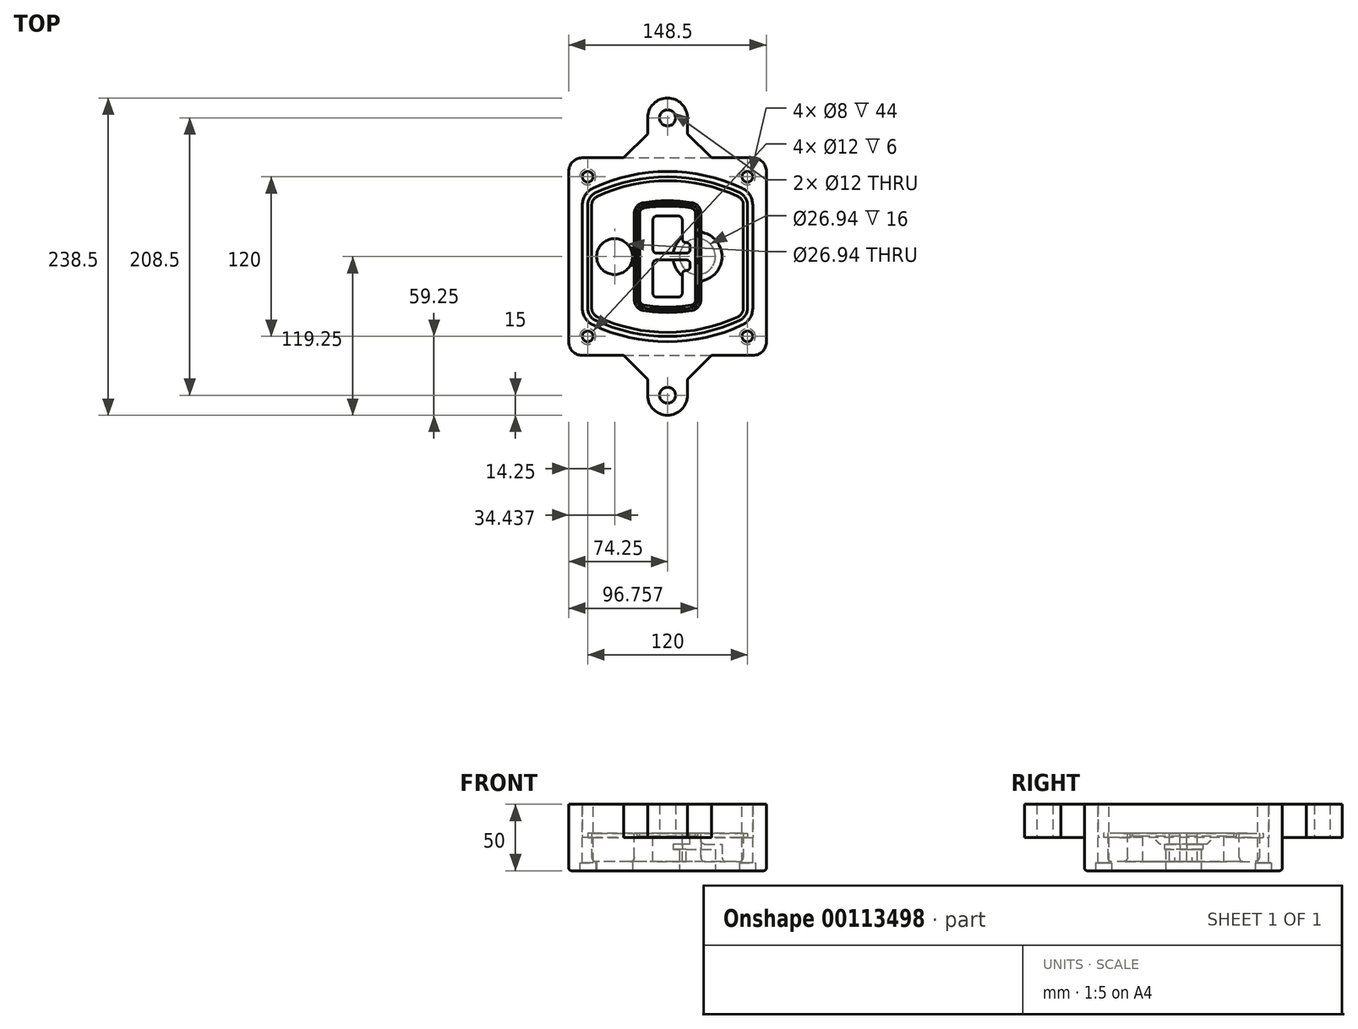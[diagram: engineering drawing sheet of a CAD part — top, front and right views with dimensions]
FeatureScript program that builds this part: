
annotation { "Feature Type Name" : "Feature", "Feature Type Description" : "" }
export const myFeature = defineFeature(function(context is Context, id is Id, definition is map)
    precondition{}
    {
        {
            var Q0;
            Q0=qCreatedBy(makeId("Top.planeOp"),FACE);
            var sketch = newSketch(context, id + "F0", { "sketchPlane" : qUnion([Q0])});
            skPoint(sketch, "E0.rect.middle", {"position": v(0, 0) * mm});
            skLineSegment(sketch, "E1.bottom", {"start": v(-64.25, -74.25) * mm, "end": v(64.25, -74.25) * mm});
            skLineSegment(sketch, "E1.top", {"start": v(-64.25, 74.25) * mm, "end": v(64.25, 74.25) * mm});
            skLineSegment(sketch, "E1.left", {"start": v(-74.25, -64.25) * mm, "end": v(-74.25, 64.25) * mm});
            skLineSegment(sketch, "E1.right", {"start": v(74.25, -64.25) * mm, "end": v(74.25, 64.25) * mm});
            skLineSegment(sketch, "E2", {"start": v(-74.25, 74.25) * mm, "end": v(74.25, -74.25) * mm, "construction": true});
            skLineSegment(sketch, "E3", {"start": v(74.25, 74.25) * mm, "end": v(-74.25, -74.25) * mm, "construction": true});
            skCircle(sketch, "E4", {"center": v(-60, 60) * mm, "radius": 4 * mm});
            skCircle(sketch, "E5", {"center": v(60, 60) * mm, "radius": 4 * mm});
            skCircle(sketch, "E6", {"center": v(60, -60) * mm, "radius": 4 * mm});
            skCircle(sketch, "E7", {"center": v(-60, -60) * mm, "radius": 4 * mm});
            skLineSegment(sketch, "E8", {"start": v(-60, 60) * mm, "end": v(60, 60) * mm, "construction": true});
            skLineSegment(sketch, "E9", {"start": v(60, 60) * mm, "end": v(60, -60) * mm, "construction": true});
            skLineSegment(sketch, "E10", {"start": v(60, -60) * mm, "end": v(-60, -60) * mm, "construction": true});
            skLineSegment(sketch, "E11", {"start": v(-60, -60) * mm, "end": v(-60, 60) * mm, "construction": true});
            skLineSegment(sketch, "E12", {"start": v(-60, 38.83) * mm, "end": v(-60, -38.83) * mm});
            skLineSegment(sketch, "E13", {"start": v(60, 38.83) * mm, "end": v(60, -38.83) * mm});
            skArc(sketch, "E14", {"start": v(54.26, 47.88) * mm, "mid": v(0, 60) * mm, "end": v(-54.26, 47.88) * mm});
            skArc(sketch, "E15", {"start": v(-54.26, -47.88) * mm, "mid": v(0, -60) * mm, "end": v(54.26, -47.88) * mm});
            skLineSegment(sketch, "E16", {"start": v(-60, 0) * mm, "end": v(60, 0) * mm, "construction": true});
            skPoint(sketch, "E17.visualSharp", {"position": v(-60, -45) * mm});
            skArc(sketch, "E17.filletArc", {"start": v(-60, -38.83) * mm, "mid": v(-58.44, -44.2) * mm, "end": v(-54.26, -47.88) * mm});
            skPoint(sketch, "E18.visualSharp", {"position": v(-60, 45) * mm});
            skArc(sketch, "E18.filletArc", {"start": v(-54.26, 47.88) * mm, "mid": v(-58.44, 44.2) * mm, "end": v(-60, 38.83) * mm});
            skPoint(sketch, "E19.visualSharp", {"position": v(60, 45) * mm});
            skArc(sketch, "E19.filletArc", {"start": v(60, 38.83) * mm, "mid": v(58.44, 44.2) * mm, "end": v(54.26, 47.88) * mm});
            skPoint(sketch, "E20.visualSharp", {"position": v(60, -45) * mm});
            skArc(sketch, "E20.filletArc", {"start": v(54.26, -47.88) * mm, "mid": v(58.44, -44.2) * mm, "end": v(60, -38.83) * mm});
            skPoint(sketch, "E21.visualSharp", {"position": v(-74.25, 74.25) * mm});
            skArc(sketch, "E21.filletArc", {"start": v(-64.25, 74.25) * mm, "mid": v(-71.32, 71.32) * mm, "end": v(-74.25, 64.25) * mm});
            skPoint(sketch, "E22.visualSharp", {"position": v(74.25, 74.25) * mm});
            skArc(sketch, "E22.filletArc", {"start": v(74.25, 64.25) * mm, "mid": v(71.32, 71.32) * mm, "end": v(64.25, 74.25) * mm});
            skPoint(sketch, "E23.visualSharp", {"position": v(74.25, -74.25) * mm});
            skArc(sketch, "E23.filletArc", {"start": v(64.25, -74.25) * mm, "mid": v(71.32, -71.32) * mm, "end": v(74.25, -64.25) * mm});
            skPoint(sketch, "E24.visualSharp", {"position": v(-74.25, -74.25) * mm});
            skArc(sketch, "E24.filletArc", {"start": v(-74.25, -64.25) * mm, "mid": v(-71.32, -71.32) * mm, "end": v(-64.25, -74.25) * mm});
            skArc(sketch, "E25.0", {"start": v(57, 38.83) * mm, "mid": v(55.9, 42.58) * mm, "end": v(52.98, 45.17) * mm});
            skLineSegment(sketch, "E25.1", {"start": v(57, 38.83) * mm, "end": v(57, -38.83) * mm});
            skArc(sketch, "E25.2", {"start": v(52.98, -45.17) * mm, "mid": v(55.9, -42.58) * mm, "end": v(57, -38.83) * mm});
            skArc(sketch, "E25.3", {"start": v(-52.98, -45.17) * mm, "mid": v(0, -57) * mm, "end": v(52.98, -45.17) * mm});
            skArc(sketch, "E25.4", {"start": v(-57, -38.83) * mm, "mid": v(-55.9, -42.58) * mm, "end": v(-52.98, -45.17) * mm});
            skArc(sketch, "E25.5", {"start": v(52.98, 45.17) * mm, "mid": v(0, 57) * mm, "end": v(-52.98, 45.17) * mm});
            skLineSegment(sketch, "E25.6", {"start": v(-57, 38.83) * mm, "end": v(-57, -38.83) * mm});
            skArc(sketch, "E25.7", {"start": v(-52.98, 45.17) * mm, "mid": v(-55.9, 42.58) * mm, "end": v(-57, 38.83) * mm});
            skArc(sketch, "E26.0", {"start": v(-55.96, 51.5) * mm, "mid": v(-61.82, 46.33) * mm, "end": v(-64, 38.83) * mm});
            skArc(sketch, "E26.1", {"start": v(55.96, 51.5) * mm, "mid": v(0, 64) * mm, "end": v(-55.96, 51.5) * mm});
            skArc(sketch, "E26.2", {"start": v(64, 38.83) * mm, "mid": v(61.82, 46.33) * mm, "end": v(55.96, 51.5) * mm});
            skLineSegment(sketch, "E26.3", {"start": v(64, 38.83) * mm, "end": v(64, -38.83) * mm});
            skArc(sketch, "E26.4", {"start": v(55.96, -51.5) * mm, "mid": v(61.82, -46.33) * mm, "end": v(64, -38.83) * mm});
            skLineSegment(sketch, "E26.5", {"start": v(-64, 38.83) * mm, "end": v(-64, -38.83) * mm});
            skArc(sketch, "E26.6", {"start": v(-55.96, -51.5) * mm, "mid": v(0, -64) * mm, "end": v(55.96, -51.5) * mm});
            skArc(sketch, "E26.7", {"start": v(-64, -38.83) * mm, "mid": v(-61.82, -46.33) * mm, "end": v(-55.96, -51.5) * mm});
            skLineSegment(sketch, "E27", {"start": v(-33, 74.25) * mm, "end": v(-15, 92.25) * mm});
            skLineSegment(sketch, "E28", {"start": v(-15, 92.25) * mm, "end": v(-15, 104.25) * mm});
            skLineSegment(sketch, "E29", {"start": v(33, 74.25) * mm, "end": v(15, 92.25) * mm});
            skLineSegment(sketch, "E30", {"start": v(15, 92.25) * mm, "end": v(15, 104.25) * mm});
            skArc(sketch, "E31", {"start": v(15, 104.25) * mm, "mid": v(0, 119.25) * mm, "end": v(-15, 104.25) * mm});
            skCircle(sketch, "E32", {"center": v(0, 104.25) * mm, "radius": 6 * mm});
            skLineSegment(sketch, "E33", {"start": v(0, 104.25) * mm, "end": v(0, 74.25) * mm, "construction": true});
            skLineSegment(sketch, "E34", {"start": v(-74.25, 0) * mm, "end": v(74.25, 0) * mm, "construction": true});
            skLineSegment(sketch, "E35.MirrorCS", {"start": v(33, -74.25) * mm, "end": v(15, -92.25) * mm});
            skLineSegment(sketch, "E36.MirrorCS", {"start": v(15, -92.25) * mm, "end": v(15, -104.25) * mm});
            skArc(sketch, "E37.MirrorCS", {"start": v(15, -104.25) * mm, "mid": v(0, -119.25) * mm, "end": v(-15, -104.25) * mm});
            skLineSegment(sketch, "E38.MirrorCS", {"start": v(-15, -92.25) * mm, "end": v(-15, -104.25) * mm});
            skLineSegment(sketch, "E39.MirrorCS", {"start": v(-33, -74.25) * mm, "end": v(-15, -92.25) * mm});
            skCircle(sketch, "E40.MirrorC", {"center": v(0, -104.25) * mm, "radius": 6 * mm});
            skLineSegment(sketch, "E41.MirrorCS", {"start": v(0, -104.25) * mm, "end": v(0, -74.25) * mm, "construction": true});
            skSolve(sketch);
        }
        {
            var Q0;
            Q0=makeQuery(id+"F0.imprint","IMPRINT",FACE,{"disambiguationData":[TD([[makeQuery(id+"F0.imprint","IMPRINT",EDGE,{"derivedFrom":sQuery(id+"F0.wireOp",EDGE,"E1.bottom")}),1.0]])]});
            var Q1;
            Q1=makeQuery(id+"F0.imprint","IMPRINT",FACE,{"disambiguationData":[TD([[makeQuery(id+"F0.imprint","IMPRINT",EDGE,{"derivedFrom":sQuery(id+"F0.wireOp",EDGE,"E12")}),1.0]])]});
            var Q2;
            Q2=makeQuery(id+"F0.imprint","IMPRINT",FACE,{"disambiguationData":[TD([[makeQuery(id+"F0.imprint","IMPRINT",EDGE,{"derivedFrom":sQuery(id+"F0.wireOp",EDGE,"E25.0")}),1.0]])]});
            var Q3;
            Q3=makeQuery(id+"F0.imprint","IMPRINT",FACE,{"disambiguationData":[TD([[makeQuery(id+"F0.imprint","IMPRINT",EDGE,{"derivedFrom":sQuery(id+"F0.wireOp",EDGE,"E12")}),-1.0]])]});
            extrude(context, id + "F1", {"entities" : qUnion([Q0, Q1, Q2, Q3]), "oppositeDirection" : true, "depth" : 25 * mm});
        }
        {
            var Q0;
            Q0=makeQuery(id+"F0.imprint","IMPRINT",FACE,{"disambiguationData":[TD([[makeQuery(id+"F0.imprint","IMPRINT",EDGE,{"derivedFrom":sQuery(id+"F0.wireOp",EDGE,"E12")}),1.0]])]});
            extrude(context, id + "F2", {"entities" : qUnion([Q0]), "operationType" : NewBodyOperationType.ADD, "depth" : 3 * mm});
        }
        {
            var Q0;
            Q0=makeQuery(id+"F0.imprint","IMPRINT",FACE,{"disambiguationData":[TD([[makeQuery(id+"F0.imprint","IMPRINT",EDGE,{"derivedFrom":sQuery(id+"F0.wireOp",EDGE,"E25.0")}),1.0]])]});
            extrude(context, id + "F3", {"entities" : qUnion([Q0]), "operationType" : NewBodyOperationType.REMOVE, "oppositeDirection" : true, "depth" : 18 * mm});
        }
        {
            var Q0;
            Q0=makeQuery(id+"F2.opExtrude","CAP_FACE",FACE,{"disambiguationData":[OSD([sQuery(id+"F0.wireOp",EDGE,"E12"),sQuery(id+"F0.wireOp",EDGE,"E13"),sQuery(id+"F0.wireOp",EDGE,"E14"),sQuery(id+"F0.wireOp",EDGE,"E15"),sQuery(id+"F0.wireOp",EDGE,"E17.filletArc"),sQuery(id+"F0.wireOp",EDGE,"E18.filletArc"),sQuery(id+"F0.wireOp",EDGE,"E19.filletArc"),sQuery(id+"F0.wireOp",EDGE,"E20.filletArc"),sQuery(id+"F0.wireOp",EDGE,"E25.0"),sQuery(id+"F0.wireOp",EDGE,"E25.1"),sQuery(id+"F0.wireOp",EDGE,"E25.2"),sQuery(id+"F0.wireOp",EDGE,"E25.3"),sQuery(id+"F0.wireOp",EDGE,"E25.4"),sQuery(id+"F0.wireOp",EDGE,"E25.5"),sQuery(id+"F0.wireOp",EDGE,"E25.6"),sQuery(id+"F0.wireOp",EDGE,"E25.7")])],"isStart":false});
            var sketch = newSketch(context, id + "F4", { "sketchPlane" : qUnion([Q0])});
            skArc(sketch, "E42.0", {"start": v(-18.34, -40.45) * mm, "mid": v(0, -42) * mm, "end": v(18.34, -40.45) * mm});
            skArc(sketch, "E43.0", {"start": v(18.34, 40.45) * mm, "mid": v(0, 42) * mm, "end": v(-18.34, 40.45) * mm});
            skLineSegment(sketch, "E44", {"start": v(-25, 32.57) * mm, "end": v(-25, -32.57) * mm});
            skLineSegment(sketch, "E45", {"start": v(25, 32.57) * mm, "end": v(25, -32.57) * mm});
            skLineSegment(sketch, "E46", {"start": v(-25, 39.1) * mm, "end": v(25, 39.1) * mm, "construction": true});
            skLineSegment(sketch, "E47", {"start": v(-25, -39.1) * mm, "end": v(25, -39.1) * mm, "construction": true});
            skPoint(sketch, "E48.visualSharp", {"position": v(-25, 39.1) * mm});
            skArc(sketch, "E48.filletArc", {"start": v(-18.34, 40.45) * mm, "mid": v(-23.11, 37.73) * mm, "end": v(-25, 32.57) * mm});
            skPoint(sketch, "E49.visualSharp", {"position": v(25, 39.1) * mm});
            skArc(sketch, "E49.filletArc", {"start": v(25, 32.57) * mm, "mid": v(23.11, 37.73) * mm, "end": v(18.34, 40.45) * mm});
            skPoint(sketch, "E50.visualSharp", {"position": v(25, -39.1) * mm});
            skArc(sketch, "E50.filletArc", {"start": v(18.34, -40.45) * mm, "mid": v(23.11, -37.73) * mm, "end": v(25, -32.57) * mm});
            skPoint(sketch, "E51.visualSharp", {"position": v(-25, -39.1) * mm});
            skArc(sketch, "E51.filletArc", {"start": v(-25, -32.57) * mm, "mid": v(-23.11, -37.73) * mm, "end": v(-18.34, -40.45) * mm});
            skArc(sketch, "E52.0", {"start": v(52.98, 45.17) * mm, "mid": v(0, 57) * mm, "end": v(-52.98, 45.17) * mm});
            skArc(sketch, "E52.1", {"start": v(-52.98, 45.17) * mm, "mid": v(-55.9, 42.58) * mm, "end": v(-57, 38.83) * mm});
            skLineSegment(sketch, "E52.2", {"start": v(-57, 38.83) * mm, "end": v(-57, -38.83) * mm});
            skArc(sketch, "E52.3", {"start": v(-57, -38.83) * mm, "mid": v(-55.9, -42.58) * mm, "end": v(-52.98, -45.17) * mm});
            skArc(sketch, "E52.4", {"start": v(-52.98, -45.17) * mm, "mid": v(0, -57) * mm, "end": v(52.98, -45.17) * mm});
            skArc(sketch, "E52.5", {"start": v(52.98, -45.17) * mm, "mid": v(55.9, -42.58) * mm, "end": v(57, -38.83) * mm});
            skLineSegment(sketch, "E52.6", {"start": v(57, 38.83) * mm, "end": v(57, -38.83) * mm});
            skArc(sketch, "E52.7", {"start": v(57, 38.83) * mm, "mid": v(55.9, 42.58) * mm, "end": v(52.98, 45.17) * mm});
            skLineSegment(sketch, "E53.0", {"start": v(23, 32.57) * mm, "end": v(23, -32.57) * mm});
            skArc(sketch, "E53.1", {"start": v(18, -38.48) * mm, "mid": v(21.58, -36.44) * mm, "end": v(23, -32.57) * mm});
            skArc(sketch, "E53.2", {"start": v(-18, -38.48) * mm, "mid": v(0, -40) * mm, "end": v(18, -38.48) * mm});
            skArc(sketch, "E53.3", {"start": v(-23, -32.57) * mm, "mid": v(-21.58, -36.44) * mm, "end": v(-18, -38.48) * mm});
            skLineSegment(sketch, "E53.4", {"start": v(-23, 32.57) * mm, "end": v(-23, -32.57) * mm});
            skArc(sketch, "E53.5", {"start": v(23, 32.57) * mm, "mid": v(21.58, 36.44) * mm, "end": v(18, 38.48) * mm});
            skArc(sketch, "E53.6", {"start": v(-18, 38.48) * mm, "mid": v(-21.58, 36.44) * mm, "end": v(-23, 32.57) * mm});
            skArc(sketch, "E53.7", {"start": v(18, 38.48) * mm, "mid": v(0, 40) * mm, "end": v(-18, 38.48) * mm});
            skArc(sketch, "E54.0", {"start": v(21, 32.57) * mm, "mid": v(20.06, 35.15) * mm, "end": v(17.67, 36.5) * mm});
            skLineSegment(sketch, "E54.1", {"start": v(21, 32.57) * mm, "end": v(21, -32.57) * mm});
            skArc(sketch, "E54.2", {"start": v(17.67, -36.5) * mm, "mid": v(20.06, -35.15) * mm, "end": v(21, -32.57) * mm});
            skArc(sketch, "E54.3", {"start": v(-17.67, -36.5) * mm, "mid": v(0, -38) * mm, "end": v(17.67, -36.5) * mm});
            skArc(sketch, "E54.4", {"start": v(-21, -32.57) * mm, "mid": v(-20.06, -35.15) * mm, "end": v(-17.67, -36.5) * mm});
            skArc(sketch, "E54.5", {"start": v(17.67, 36.5) * mm, "mid": v(0, 38) * mm, "end": v(-17.67, 36.5) * mm});
            skLineSegment(sketch, "E54.6", {"start": v(-21, 32.57) * mm, "end": v(-21, -32.57) * mm});
            skArc(sketch, "E54.7", {"start": v(-17.67, 36.5) * mm, "mid": v(-20.06, 35.15) * mm, "end": v(-21, 32.57) * mm});
            skLineSegment(sketch, "E55", {"start": v(-25, 0) * mm, "end": v(25, 0) * mm, "construction": true});
            skLineSegment(sketch, "E56", {"start": v(-11, 5.5) * mm, "end": v(-11, 27.5) * mm});
            skLineSegment(sketch, "E57", {"start": v(-8, 30.5) * mm, "end": v(8, 30.5) * mm});
            skLineSegment(sketch, "E58", {"start": v(11, 27.5) * mm, "end": v(11, 13.5) * mm});
            skLineSegment(sketch, "E59", {"start": v(14, 10.5) * mm, "end": v(14, 10.5) * mm});
            skLineSegment(sketch, "E60", {"start": v(17, 7.5) * mm, "end": v(17, 5.5) * mm});
            skLineSegment(sketch, "E61", {"start": v(14, 2.5) * mm, "end": v(-8, 2.5) * mm});
            skPoint(sketch, "E62.visualSharp", {"position": v(-11, 30.5) * mm});
            skArc(sketch, "E62.filletArc", {"start": v(-8, 30.5) * mm, "mid": v(-10.12, 29.62) * mm, "end": v(-11, 27.5) * mm});
            skPoint(sketch, "E63.visualSharp", {"position": v(11, 30.5) * mm});
            skArc(sketch, "E63.filletArc", {"start": v(11, 27.5) * mm, "mid": v(10.12, 29.62) * mm, "end": v(8, 30.5) * mm});
            skPoint(sketch, "E64.visualSharp", {"position": v(11, 10.5) * mm});
            skArc(sketch, "E64.filletArc", {"start": v(11, 13.5) * mm, "mid": v(11.88, 11.38) * mm, "end": v(14, 10.5) * mm});
            skPoint(sketch, "E65.visualSharp", {"position": v(17, 10.5) * mm});
            skArc(sketch, "E65.filletArc", {"start": v(17, 7.5) * mm, "mid": v(16.12, 9.62) * mm, "end": v(14, 10.5) * mm});
            skPoint(sketch, "E66.visualSharp", {"position": v(17, 2.5) * mm});
            skArc(sketch, "E66.filletArc", {"start": v(14, 2.5) * mm, "mid": v(16.12, 3.38) * mm, "end": v(17, 5.5) * mm});
            skPoint(sketch, "E67.visualSharp", {"position": v(-11, 2.5) * mm});
            skArc(sketch, "E67.filletArc", {"start": v(-11, 5.5) * mm, "mid": v(-10.12, 3.38) * mm, "end": v(-8, 2.5) * mm});
            skLineSegment(sketch, "E68.0.MirrorCS", {"start": v(14, -2.5) * mm, "end": v(-8, -2.5) * mm});
            skArc(sketch, "E69.0.MirrorCS", {"start": v(-11, -5.5) * mm, "mid": v(-10.12, -3.38) * mm, "end": v(-8, -2.5) * mm});
            skLineSegment(sketch, "E70.0.MirrorCS", {"start": v(-11, -5.5) * mm, "end": v(-11, -27.5) * mm});
            skArc(sketch, "E71.0.MirrorCS", {"start": v(-8, -30.5) * mm, "mid": v(-10.12, -29.62) * mm, "end": v(-11, -27.5) * mm});
            skLineSegment(sketch, "E72.0.MirrorCS", {"start": v(-8, -30.5) * mm, "end": v(8, -30.5) * mm});
            skArc(sketch, "E73.0.MirrorCS", {"start": v(11, -27.5) * mm, "mid": v(10.12, -29.62) * mm, "end": v(8, -30.5) * mm});
            skLineSegment(sketch, "E74.0.MirrorCS", {"start": v(11, -27.5) * mm, "end": v(11, -13.5) * mm});
            skArc(sketch, "E75.0.MirrorCS", {"start": v(11, -13.5) * mm, "mid": v(11.88, -11.38) * mm, "end": v(14, -10.5) * mm});
            skArc(sketch, "E76.0.MirrorCS", {"start": v(17, -7.5) * mm, "mid": v(16.12, -9.62) * mm, "end": v(14, -10.5) * mm});
            skLineSegment(sketch, "E77.0.MirrorCS", {"start": v(17, -7.5) * mm, "end": v(17, -5.5) * mm});
            skArc(sketch, "E78.0.MirrorCS", {"start": v(14, -2.5) * mm, "mid": v(16.12, -3.38) * mm, "end": v(17, -5.5) * mm});
            skSolve(sketch);
        }
        {
            var Q0;
            Q0=makeQuery(id+"F4.imprint","IMPRINT",FACE,{"disambiguationData":[TD([[makeQuery(id+"F4.imprint","IMPRINT",EDGE,{"derivedFrom":sQuery(id+"F4.wireOp",EDGE,"E42.0")}),1.0]])]});
            var Q1;
            Q1=makeQuery(id+"F4.imprint","IMPRINT",FACE,{"disambiguationData":[TD([[makeQuery(id+"F4.imprint","IMPRINT",EDGE,{"derivedFrom":sQuery(id+"F4.wireOp",EDGE,"E53.0")}),-1.0]])]});
            var Q2;
            Q2=makeQuery(id+"F4.imprint","IMPRINT",FACE,{"disambiguationData":[TD([[makeQuery(id+"F4.imprint","IMPRINT",EDGE,{"derivedFrom":sQuery(id+"F4.wireOp",EDGE,"E54.0")}),1.0]])]});
            extrude(context, id + "F5", {"entities" : qUnion([Q0, Q1, Q2]), "operationType" : NewBodyOperationType.ADD, "endBound" : BoundingType.UP_TO_NEXT, "oppositeDirection" : true, "depth" : 25 * mm});
        }
        {
            var Q0;
            Q0=makeQuery(id+"F4.imprint","IMPRINT",FACE,{"disambiguationData":[TD([[makeQuery(id+"F4.imprint","IMPRINT",EDGE,{"derivedFrom":sQuery(id+"F4.wireOp",EDGE,"E53.0")}),-1.0]])]});
            extrude(context, id + "F6", {"entities" : qUnion([Q0]), "operationType" : NewBodyOperationType.REMOVE, "oppositeDirection" : true, "depth" : 2 * mm});
        }
        {
            var Q0;
            Q0=makeQuery(id+"F1.opExtrude","CAP_FACE",FACE,{"disambiguationData":[OSD([sQuery(id+"F0.wireOp",EDGE,"E1.bottom"),sQuery(id+"F0.wireOp",EDGE,"E1.top"),sQuery(id+"F0.wireOp",EDGE,"E1.left"),sQuery(id+"F0.wireOp",EDGE,"E1.right"),sQuery(id+"F0.wireOp",EDGE,"E4"),sQuery(id+"F0.wireOp",EDGE,"E5"),sQuery(id+"F0.wireOp",EDGE,"E6"),sQuery(id+"F0.wireOp",EDGE,"E7"),sQuery(id+"F0.wireOp",EDGE,"E21.filletArc"),sQuery(id+"F0.wireOp",EDGE,"E22.filletArc"),sQuery(id+"F0.wireOp",EDGE,"E23.filletArc"),sQuery(id+"F0.wireOp",EDGE,"E24.filletArc")])],"isStart":false});
            var sketch = newSketch(context, id + "F7", { "sketchPlane" : qUnion([Q0])});
            skCircle(sketch, "E79", {"center": v(22.5, 0) * mm, "radius": 13.47 * mm});
            skCircle(sketch, "E80", {"center": v(-39.81, 0) * mm, "radius": 13.47 * mm});
            skLineSegment(sketch, "E81", {"start": v(74.25, 0) * mm, "end": v(-74.25, 0) * mm});
            skCircle(sketch, "E82", {"center": v(22.5, 0) * mm, "radius": 18.47 * mm});
            skCircle(sketch, "E83", {"center": v(60, -60) * mm, "radius": 6 * mm});
            skCircle(sketch, "E84", {"center": v(-60, -60) * mm, "radius": 6 * mm});
            skCircle(sketch, "E85", {"center": v(-60, 60) * mm, "radius": 6 * mm});
            skCircle(sketch, "E86", {"center": v(60, 60) * mm, "radius": 6 * mm});
            skSolve(sketch);
        }
        {
            var Q0;
            {var subQ1=sQuery(id+"F7.wireOp",EDGE,"E81");var subQ4=sQuery(id+"F7.wireOp",EDGE,"E79");var subQ6=makeQuery(id+"F7.imprint","INTERSECT",VERTEX,{"disambiguationData":[OD(0.0)],"derivedFrom":[subQ4,subQ1]});Q0=makeQuery(id+"F7.imprint","IMPRINT",FACE,{"disambiguationData":[TD([[makeQuery(id+"F7.imprint","IMPRINT",EDGE,{"disambiguationData":[TD([[subQ6,-1.0]])],"derivedFrom":subQ4}),-1.0]])]});}
            var Q1;
            {var subQ0=sQuery(id+"F7.wireOp",EDGE,"E81");var subQ1=sQuery(id+"F7.wireOp",EDGE,"E79");var subQ3=makeQuery(id+"F7.imprint","INTERSECT",VERTEX,{"disambiguationData":[OD(0.0)],"derivedFrom":[subQ1,subQ0]});Q1=makeQuery(id+"F7.imprint","IMPRINT",FACE,{"disambiguationData":[TD([[makeQuery(id+"F7.imprint","IMPRINT",EDGE,{"disambiguationData":[TD([[subQ3,-1.0]])],"derivedFrom":subQ1}),1.0]])]});}
            var Q2;
            {var subQ0=sQuery(id+"F7.wireOp",EDGE,"E81");var subQ1=sQuery(id+"F7.wireOp",EDGE,"E79");var subQ3=makeQuery(id+"F7.imprint","INTERSECT",VERTEX,{"disambiguationData":[OD(0.0)],"derivedFrom":[subQ1,subQ0]});Q2=makeQuery(id+"F7.imprint","IMPRINT",FACE,{"disambiguationData":[TD([[makeQuery(id+"F7.imprint","IMPRINT",EDGE,{"disambiguationData":[TD([[subQ3,1.0]])],"derivedFrom":subQ1}),1.0]])]});}
            var Q3;
            {var subQ1=sQuery(id+"F7.wireOp",EDGE,"E81");var subQ4=sQuery(id+"F7.wireOp",EDGE,"E79");var subQ6=makeQuery(id+"F7.imprint","INTERSECT",VERTEX,{"disambiguationData":[OD(0.0)],"derivedFrom":[subQ4,subQ1]});Q3=makeQuery(id+"F7.imprint","IMPRINT",FACE,{"disambiguationData":[TD([[makeQuery(id+"F7.imprint","IMPRINT",EDGE,{"disambiguationData":[TD([[subQ6,1.0]])],"derivedFrom":subQ4}),-1.0]])]});}
            extrude(context, id + "F8", {"entities" : qUnion([Q0, Q1, Q2, Q3]), "operationType" : NewBodyOperationType.ADD, "oppositeDirection" : true, "depth" : 20 * mm});
        }
        {
            var Q0;
            {var subQ0=sQuery(id+"F7.wireOp",EDGE,"E81");var subQ1=sQuery(id+"F7.wireOp",EDGE,"E79");var subQ3=makeQuery(id+"F7.imprint","INTERSECT",VERTEX,{"disambiguationData":[OD(0.0)],"derivedFrom":[subQ1,subQ0]});Q0=makeQuery(id+"F7.imprint","IMPRINT",FACE,{"disambiguationData":[TD([[makeQuery(id+"F7.imprint","IMPRINT",EDGE,{"disambiguationData":[TD([[subQ3,-1.0]])],"derivedFrom":subQ1}),1.0]])]});}
            var Q1;
            {var subQ0=sQuery(id+"F7.wireOp",EDGE,"E81");var subQ1=sQuery(id+"F7.wireOp",EDGE,"E79");var subQ3=makeQuery(id+"F7.imprint","INTERSECT",VERTEX,{"disambiguationData":[OD(0.0)],"derivedFrom":[subQ1,subQ0]});Q1=makeQuery(id+"F7.imprint","IMPRINT",FACE,{"disambiguationData":[TD([[makeQuery(id+"F7.imprint","IMPRINT",EDGE,{"disambiguationData":[TD([[subQ3,1.0]])],"derivedFrom":subQ1}),1.0]])]});}
            extrude(context, id + "F9", {"entities" : qUnion([Q0, Q1]), "operationType" : NewBodyOperationType.REMOVE, "oppositeDirection" : true, "depth" : 16 * mm});
        }
        {
            var Q0;
            {var subQ0=sQuery(id+"F7.wireOp",EDGE,"E81");var subQ1=sQuery(id+"F7.wireOp",EDGE,"E80");var subQ3=makeQuery(id+"F7.imprint","INTERSECT",VERTEX,{"disambiguationData":[OD(0.0)],"derivedFrom":[subQ1,subQ0]});Q0=makeQuery(id+"F7.imprint","IMPRINT",FACE,{"disambiguationData":[TD([[makeQuery(id+"F7.imprint","IMPRINT",EDGE,{"disambiguationData":[TD([[subQ3,-1.0]])],"derivedFrom":subQ1}),1.0]])]});}
            var Q1;
            {var subQ0=sQuery(id+"F7.wireOp",EDGE,"E81");var subQ1=sQuery(id+"F7.wireOp",EDGE,"E80");var subQ3=makeQuery(id+"F7.imprint","INTERSECT",VERTEX,{"disambiguationData":[OD(0.0)],"derivedFrom":[subQ1,subQ0]});Q1=makeQuery(id+"F7.imprint","IMPRINT",FACE,{"disambiguationData":[TD([[makeQuery(id+"F7.imprint","IMPRINT",EDGE,{"disambiguationData":[TD([[subQ3,1.0]])],"derivedFrom":subQ1}),1.0]])]});}
            extrude(context, id + "F10", {"entities" : qUnion([Q0, Q1]), "operationType" : NewBodyOperationType.REMOVE, "oppositeDirection" : true, "depth" : 25 * mm});
        }
        {
            var Q0;
            Q0=makeQuery(id+"F7.imprint","IMPRINT",FACE,{"disambiguationData":[TD([[makeQuery(id+"F7.imprint","IMPRINT",EDGE,{"derivedFrom":sQuery(id+"F7.wireOp",EDGE,"E83")}),1.0]])]});
            var Q1;
            Q1=makeQuery(id+"F7.imprint","IMPRINT",FACE,{"disambiguationData":[TD([[makeQuery(id+"F7.imprint","IMPRINT",EDGE,{"derivedFrom":makeQuery(id+"F1.opExtrude","CAP_EDGE",EDGE,{"disambiguationData":[OSD([sQuery(id+"F0.wireOp",EDGE,"E5")])],"isStart":false})}),-1.0]])]});
            var Q2;
            Q2=makeQuery(id+"F7.imprint","IMPRINT",FACE,{"disambiguationData":[TD([[makeQuery(id+"F7.imprint","IMPRINT",EDGE,{"derivedFrom":sQuery(id+"F7.wireOp",EDGE,"E84")}),1.0]])]});
            var Q3;
            Q3=makeQuery(id+"F7.imprint","IMPRINT",FACE,{"disambiguationData":[TD([[makeQuery(id+"F7.imprint","IMPRINT",EDGE,{"derivedFrom":makeQuery(id+"F1.opExtrude","CAP_EDGE",EDGE,{"disambiguationData":[OSD([sQuery(id+"F0.wireOp",EDGE,"E4")])],"isStart":false})}),-1.0]])]});
            var Q4;
            Q4=makeQuery(id+"F7.imprint","IMPRINT",FACE,{"disambiguationData":[TD([[makeQuery(id+"F7.imprint","IMPRINT",EDGE,{"derivedFrom":sQuery(id+"F7.wireOp",EDGE,"E85")}),1.0]])]});
            var Q5;
            Q5=makeQuery(id+"F7.imprint","IMPRINT",FACE,{"disambiguationData":[TD([[makeQuery(id+"F7.imprint","IMPRINT",EDGE,{"derivedFrom":makeQuery(id+"F1.opExtrude","CAP_EDGE",EDGE,{"disambiguationData":[OSD([sQuery(id+"F0.wireOp",EDGE,"E7")])],"isStart":false})}),-1.0]])]});
            var Q6;
            Q6=makeQuery(id+"F7.imprint","IMPRINT",FACE,{"disambiguationData":[TD([[makeQuery(id+"F7.imprint","IMPRINT",EDGE,{"derivedFrom":sQuery(id+"F7.wireOp",EDGE,"E86")}),1.0]])]});
            var Q7;
            Q7=makeQuery(id+"F7.imprint","IMPRINT",FACE,{"disambiguationData":[TD([[makeQuery(id+"F7.imprint","IMPRINT",EDGE,{"derivedFrom":makeQuery(id+"F1.opExtrude","CAP_EDGE",EDGE,{"disambiguationData":[OSD([sQuery(id+"F0.wireOp",EDGE,"E6")])],"isStart":false})}),-1.0]])]});
            extrude(context, id + "F11", {"entities" : qUnion([Q0, Q1, Q2, Q3, Q4, Q5, Q6, Q7]), "operationType" : NewBodyOperationType.REMOVE, "oppositeDirection" : true, "depth" : 6 * mm});
        }
        {
            var Q0;
            Q0=makeQuery(id+"F9.boolean.opBoolean","COPY",FACE,{"derivedFrom":makeQuery(id+"F9.opExtrude","CAP_FACE",FACE,{"disambiguationData":[OSD([sQuery(id+"F7.wireOp",EDGE,"E79")])],"isStart":false})});
            var sketch = newSketch(context, id + "F12", { "sketchPlane" : qUnion([Q0])});
            skArc(sketch, "E87.0", {"start": v(11, 14.45) * mm, "mid": v(6.45, 9.13) * mm, "end": v(4.2, 2.5) * mm});
            skArc(sketch, "E87.1", {"start": v(4.2, -2.5) * mm, "mid": v(6.45, -9.13) * mm, "end": v(11, -14.45) * mm});
            skLineSegment(sketch, "E88", {"start": v(4.2, -2.5) * mm, "end": v(14, -2.5) * mm});
            skLineSegment(sketch, "E89.0", {"start": v(14, 2.5) * mm, "end": v(4.2, 2.5) * mm});
            skArc(sketch, "E89.1", {"start": v(14, 2.5) * mm, "mid": v(16.12, 3.38) * mm, "end": v(17, 5.5) * mm});
            skLineSegment(sketch, "E89.2", {"start": v(17, 7.5) * mm, "end": v(17, 5.5) * mm});
            skArc(sketch, "E89.3", {"start": v(17, 7.5) * mm, "mid": v(16.12, 9.62) * mm, "end": v(14, 10.5) * mm});
            skArc(sketch, "E89.4", {"start": v(11, 13.5) * mm, "mid": v(11.88, 11.38) * mm, "end": v(14, 10.5) * mm});
            skLineSegment(sketch, "E89.5", {"start": v(11, 14.45) * mm, "end": v(11, 13.5) * mm});
            skLineSegment(sketch, "E89.7", {"start": v(14, -2.5) * mm, "end": v(4.2, -2.5) * mm});
            skArc(sketch, "E89.8", {"start": v(14, -2.5) * mm, "mid": v(16.12, -3.38) * mm, "end": v(17, -5.5) * mm});
            skLineSegment(sketch, "E89.9", {"start": v(17, -7.5) * mm, "end": v(17, -5.5) * mm});
            skArc(sketch, "E89.10", {"start": v(17, -7.5) * mm, "mid": v(16.12, -9.62) * mm, "end": v(14, -10.5) * mm});
            skArc(sketch, "E89.11", {"start": v(11, -13.5) * mm, "mid": v(11.88, -11.38) * mm, "end": v(14, -10.5) * mm});
            skLineSegment(sketch, "E89.12", {"start": v(11, -14.45) * mm, "end": v(11, -13.5) * mm});
            skPoint(sketch, "E90.orphan", {"position": v(11, -27.5) * mm});
            skPoint(sketch, "E91.orphan", {"position": v(-8, -2.5) * mm});
            skPoint(sketch, "E92.orphan", {"position": v(-8, 2.5) * mm});
            skPoint(sketch, "E93.orphan", {"position": v(11, 27.5) * mm});
            skSolve(sketch);
        }
        {
            var Q0;
            {var subQ7=sQuery(id+"F12.wireOp",EDGE,"E87.0");var subQ14=sQuery(id+"F12.wireOp",EDGE,"E87.1");var subQ16=sQuery(id+"F12.wireOp",EDGE,"E89.1");var subQ18=sQuery(id+"F12.wireOp",EDGE,"E89.8");Q0=qUnion([makeQuery(id+"F12.imprint","IMPRINT",FACE,{"disambiguationData":[TD([[makeQuery(id+"F12.imprint","IMPRINT",EDGE,{"derivedFrom":subQ7}),1.0]])]}),makeQuery(id+"F12.imprint","IMPRINT",FACE,{"disambiguationData":[TD([[makeQuery(id+"F12.imprint","IMPRINT",EDGE,{"derivedFrom":subQ14}),1.0]])]}),makeQuery(id+"F12.imprint","IMPRINT",FACE,{"disambiguationData":[TD([[makeQuery(id+"F12.imprint","IMPRINT",EDGE,{"derivedFrom":subQ16}),1.0]])]}),makeQuery(id+"F12.imprint","IMPRINT",FACE,{"disambiguationData":[TD([[makeQuery(id+"F12.imprint","IMPRINT",EDGE,{"derivedFrom":subQ18}),-1.0]])]})]);}
            var Q1;
            Q1=makeQuery(id+"F5.boolean.opBoolean","SPLIT",FACE,{"disambiguationData":[TD([makeQuery(id+"F5.opExtrude","SWEPT_FACE",FACE,{"disambiguationData":[OSD([sQuery(id+"F4.wireOp",EDGE,"E56")])]})])],"derivedFrom":makeQuery(id+"F3.boolean.opBoolean","COPY",FACE,{"derivedFrom":makeQuery(id+"F3.opExtrude","CAP_FACE",FACE,{"disambiguationData":[OSD([sQuery(id+"F0.wireOp",EDGE,"E25.0"),sQuery(id+"F0.wireOp",EDGE,"E25.1"),sQuery(id+"F0.wireOp",EDGE,"E25.2"),sQuery(id+"F0.wireOp",EDGE,"E25.3"),sQuery(id+"F0.wireOp",EDGE,"E25.4"),sQuery(id+"F0.wireOp",EDGE,"E25.5"),sQuery(id+"F0.wireOp",EDGE,"E25.6"),sQuery(id+"F0.wireOp",EDGE,"E25.7")])],"isStart":false})})});
            extrude(context, id + "F13", {"entities" : qUnion([Q0]), "operationType" : NewBodyOperationType.REMOVE, "endBound" : BoundingType.UP_TO_SURFACE, "endBoundEntityFace" : qUnion([Q1]), "depth" : 25 * mm});
        }
        {
            var Q0;
            Q0=makeQuery(id+"F3.boolean.opBoolean","COPY",EDGE,{"derivedFrom":makeQuery(id+"F3.opExtrude","CAP_EDGE",EDGE,{"disambiguationData":[OSD([sQuery(id+"F0.wireOp",EDGE,"E25.6")])],"isStart":false})});
            var Q1;
            Q1=makeQuery(id+"F8.boolean.opBoolean","INTERSECT",EDGE,{"derivedFrom":[makeQuery(id+"F5.opExtrude","SWEPT_FACE",FACE,{"disambiguationData":[OSD([sQuery(id+"F4.wireOp",EDGE,"E45")])]}),makeQuery(id+"F8.opExtrude","CAP_FACE",FACE,{"disambiguationData":[OSD([sQuery(id+"F7.wireOp",EDGE,"E82")])],"isStart":false})]});
            var Q2;
            Q2=makeQuery(id+"F8.boolean.opBoolean","INTERSECT",EDGE,{"disambiguationData":[OD(1.0)],"derivedFrom":[makeQuery(id+"F5.opExtrude","SWEPT_FACE",FACE,{"disambiguationData":[OSD([sQuery(id+"F4.wireOp",EDGE,"E45")])]}),makeQuery(id+"F8.opExtrude","SWEPT_FACE",FACE,{"disambiguationData":[OSD([sQuery(id+"F7.wireOp",EDGE,"E82")])]})]});
            var Q3;
            {var subQ0=sQuery(id+"F4.wireOp",EDGE,"E45");Q3=makeQuery(id+"F8.boolean.opBoolean","SPLIT",EDGE,{"disambiguationData":[TD([makeQuery(id+"F5.opExtrude","SWEPT_FACE",FACE,{"disambiguationData":[OSD([sQuery(id+"F4.wireOp",EDGE,"E50.filletArc")])]})])],"derivedFrom":makeQuery(id+"F5.opExtrude","CAP_EDGE",EDGE,{"disambiguationData":[OSD([subQ0])],"isStart":false})});}
            var Q4;
            {var subQ0=sQuery(id+"F0.wireOp",EDGE,"E25.7");var subQ1=sQuery(id+"F0.wireOp",EDGE,"E25.1");var subQ2=sQuery(id+"F0.wireOp",EDGE,"E25.6");var subQ3=sQuery(id+"F0.wireOp",EDGE,"E25.5");var subQ4=sQuery(id+"F0.wireOp",EDGE,"E25.4");var subQ5=sQuery(id+"F0.wireOp",EDGE,"E25.0");var subQ6=sQuery(id+"F0.wireOp",EDGE,"E25.2");var subQ7=sQuery(id+"F0.wireOp",EDGE,"E25.3");Q4=makeQuery(id+"F8.boolean.opBoolean","INTERSECT",EDGE,{"derivedFrom":[makeQuery(id+"F5.boolean.opBoolean","SPLIT",FACE,{"disambiguationData":[TD([makeQuery(id+"F2.opExtrude","SWEPT_FACE",FACE,{"disambiguationData":[OSD([subQ5])]})])],"derivedFrom":makeQuery(id+"F3.boolean.opBoolean","COPY",FACE,{"derivedFrom":makeQuery(id+"F3.opExtrude","CAP_FACE",FACE,{"disambiguationData":[OSD([subQ5,subQ1,subQ6,subQ7,subQ4,subQ3,subQ2,subQ0])],"isStart":false})})}),makeQuery(id+"F8.opExtrude","SWEPT_FACE",FACE,{"disambiguationData":[OSD([sQuery(id+"F7.wireOp",EDGE,"E82")])]})]});}
            var Q5;
            Q5=makeQuery(id+"F8.boolean.opBoolean","INTERSECT",EDGE,{"disambiguationData":[OD(0.0)],"derivedFrom":[makeQuery(id+"F5.opExtrude","SWEPT_FACE",FACE,{"disambiguationData":[OSD([sQuery(id+"F4.wireOp",EDGE,"E45")])]}),makeQuery(id+"F8.opExtrude","SWEPT_FACE",FACE,{"disambiguationData":[OSD([sQuery(id+"F7.wireOp",EDGE,"E82")])]})]});
            fillet(context, id + "F14", {"entities" : qUnion([Q0, Q1, Q2, Q3, Q4, Q5]), "radius" : 3 * mm, "tangentPropagation" : true, "allowEdgeOverflow" : false});
        }
        {
            var Q0;
            Q0=makeQuery(id+"F1.opExtrude","CAP_EDGE",EDGE,{"disambiguationData":[OSD([sQuery(id+"F0.wireOp",EDGE,"E1.bottom")])],"isStart":false});
            fillet(context, id + "F15", {"entities" : qUnion([Q0]), "radius" : 2 * mm, "tangentPropagation" : true, "allowEdgeOverflow" : false});
        }
        {
            var Q0;
            Q0 = qSketchRegion(id + "F0", true);
            extrude(context, id + "F16", {"entities" : qUnion([Q0]), "operationType" : NewBodyOperationType.ADD, "depth" : 25 * mm});
        }
    });
